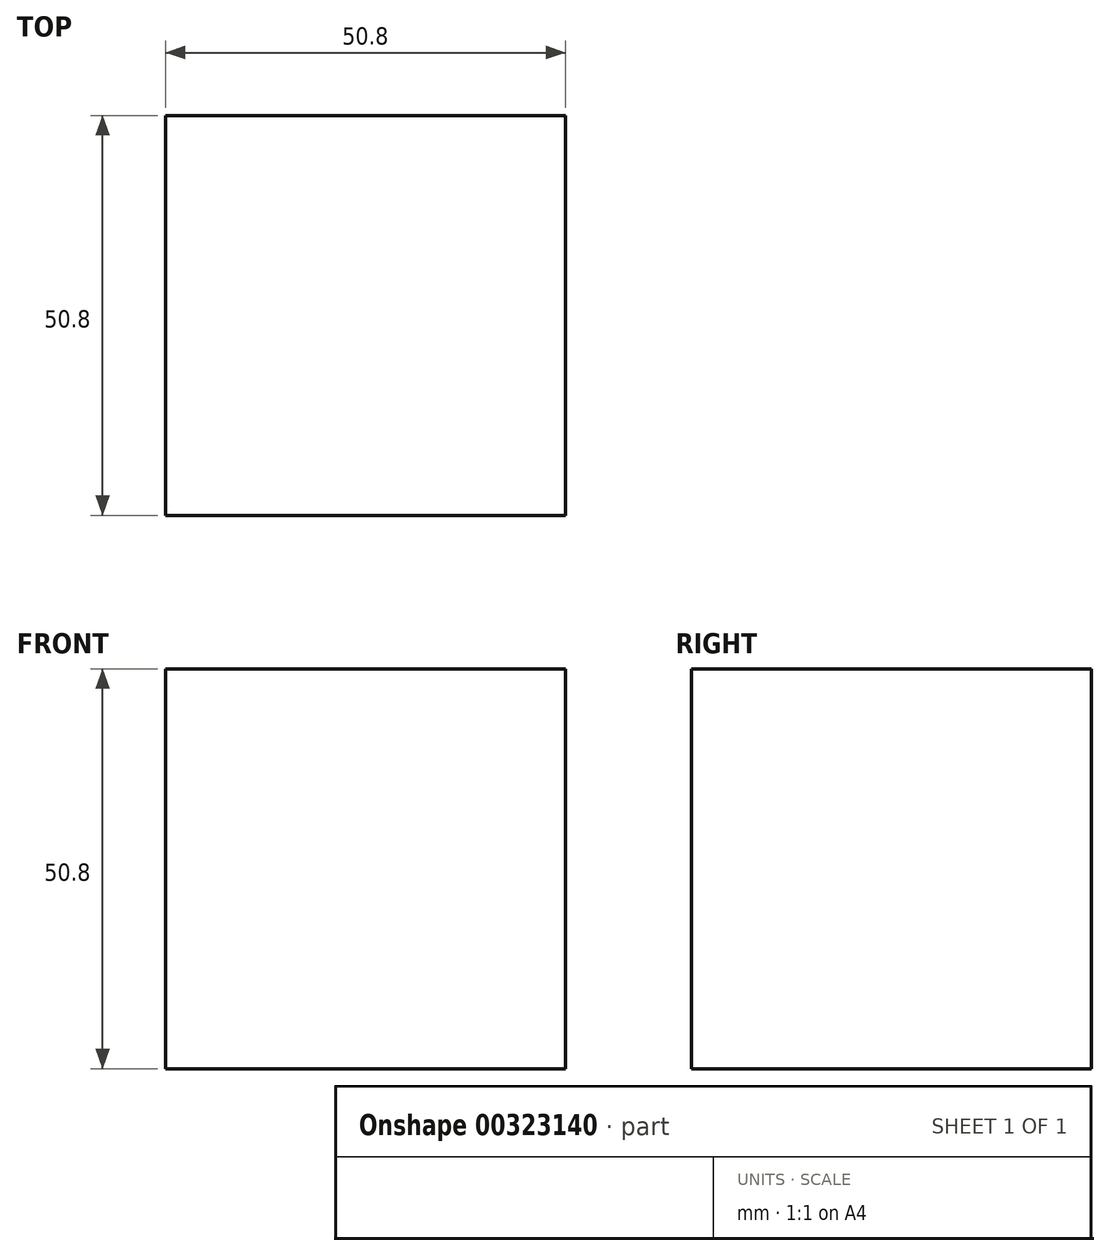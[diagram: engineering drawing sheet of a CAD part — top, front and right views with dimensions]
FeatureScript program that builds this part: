
annotation { "Feature Type Name" : "Feature", "Feature Type Description" : "" }
export const myFeature = defineFeature(function(context is Context, id is Id, definition is map)
    precondition{}
    {
        {
            var Q0;
            Q0=qCreatedBy(makeId("Top.planeOp"),FACE);
            var sketch = newSketch(context, id + "F0", { "sketchPlane" : qUnion([Q0])});
            skLineSegment(sketch, "E0", {"start": v(-19.89, 24.33) * mm, "end": v(30.91, 24.33) * mm});
            skLineSegment(sketch, "E1", {"start": v(30.91, 24.33) * mm, "end": v(30.91, -26.47) * mm});
            skLineSegment(sketch, "E2", {"start": v(30.91, -26.47) * mm, "end": v(-19.89, -26.47) * mm});
            skLineSegment(sketch, "E3", {"start": v(-19.89, -26.47) * mm, "end": v(-19.89, 24.33) * mm});
            skSolve(sketch);
        }
        {
            var Q0;
            Q0 = qSketchRegion(id + "F0", true);
            extrude(context, id + "F1", {"entities" : qUnion([Q0]), "depth" : 50.8 * mm});
        }
    });
